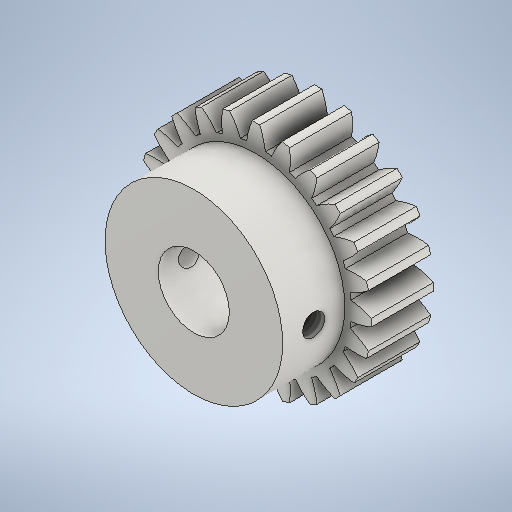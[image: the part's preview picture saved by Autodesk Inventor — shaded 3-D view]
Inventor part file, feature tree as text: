
AUTODESK INVENTOR PART (.ipt)
format: ipt  version: 2025.1 (Build 291241000, 241)  size: 459,264 bytes
history: native  units: mm (DEFAULTED — no unit token found)
features: sketch x5, plane x4, other x3, extrude x2, hole x2
ambient origin geometry x8: Origin, YZ Plane, XZ Plane, XY Plane, X Axis, Y Axis, Z Axis, Center Point
bodies: Solid1 (feature_tree)
feature tree (16):
  extrude  "Extrusion1"  Depth=7.0mm TaperAngle=0.0deg
  plane  "Work Plane2"
  plane  "Work Plane8"
  plane  "Work Plane9"
  other  "Stirnzahnrad"
  extrude  "Extrusion2"  Depth=10.0mm TaperAngle=0.0deg
  sketch  "Skizze6"  dims[d39=0.0mm d41=0.0mm]
  plane  "Arbeitsebene11"
  hole  "Bohrung2"  [1 undecoded]
  hole  "Bohrung1"  [1 undecoded]
  sketch  "Sketch1"  dims[d0=26.0mm d1=7.0mm d2=0.0mm]
  other  "Srf1"
  sketch  "Skizze4"  dims[d3=24.0mm d4=10.0mm d5=0.0mm]
  sketch  "Skizze5"  dims[d16=42.0mm d17=0.0mm d34=1.308997mm]
  sketch  "Skizze7"  dims[d43=42.0mm d46=42.0mm d47=0.0mm d48=0.0mm d50=20.0mm d51=7.0mm d52=0.0mm d54=8.0mm d55=6.0mm d56=4.0mm d57=2.0mm d58=90.0deg d59=7.0mm d60=0.0mm d61=24.0mm d62=10.0mm d63=3.5mm d64=2.459mm d65=6.0mm d66=4.0mm d67=2.0mm d68=90.0deg d69=8.0mm d70=0.0mm]
  other  "Flankendurchmesser"
note: 2 required parameter values undecoded (feature->parameter linkage not recoverable at this tier; creation-order binding heuristic only, values carry confidence <= 0.55)
